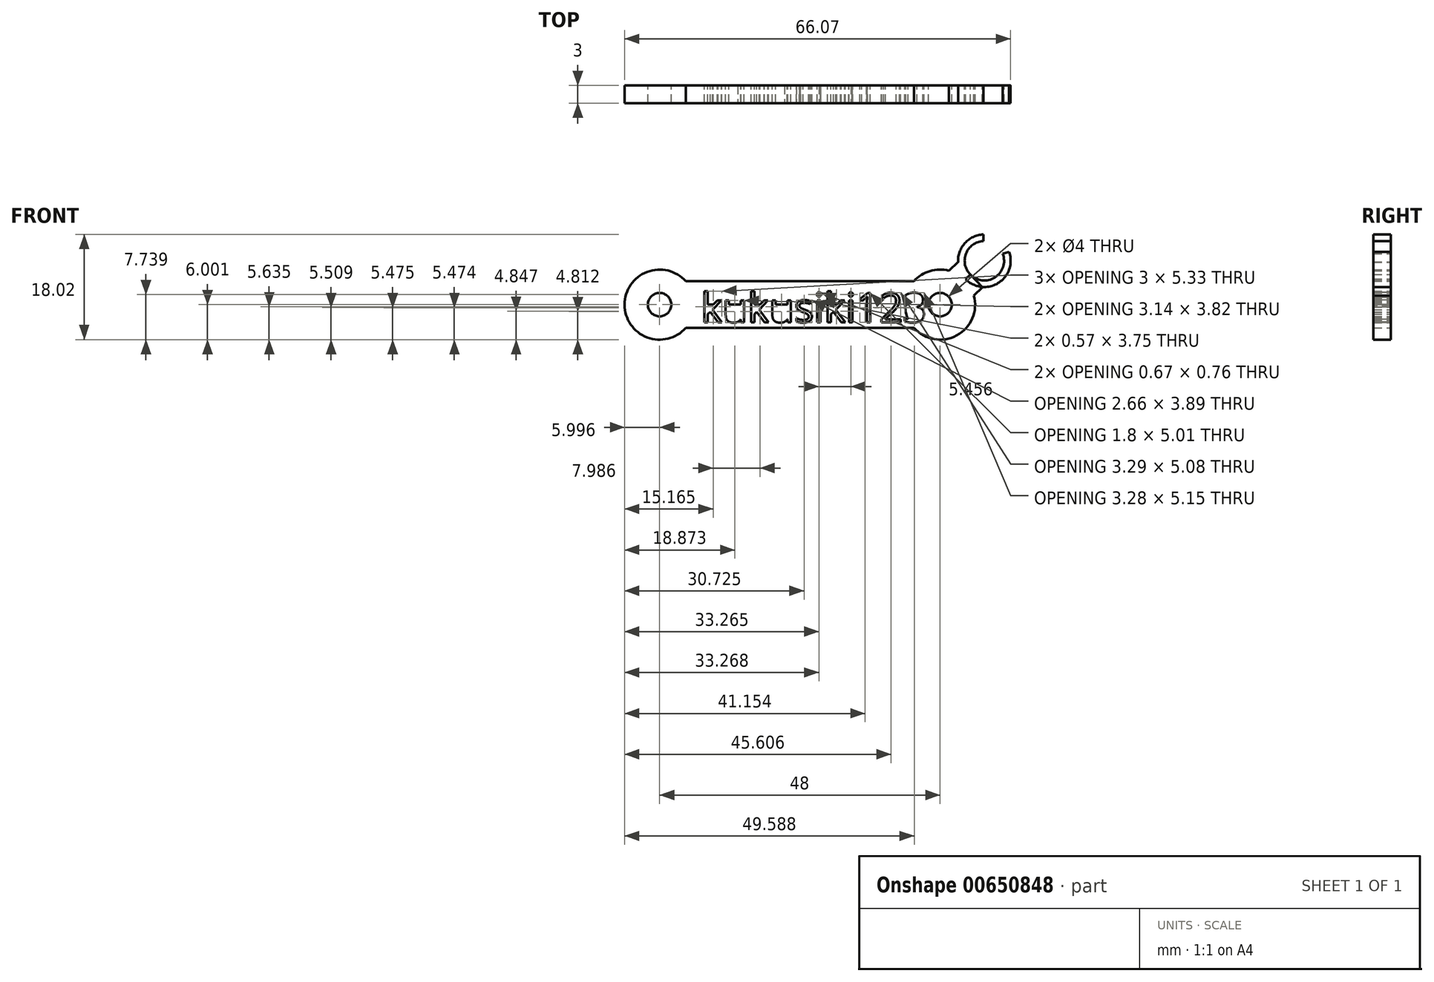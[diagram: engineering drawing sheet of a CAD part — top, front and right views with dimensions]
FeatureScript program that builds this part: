
annotation { "Feature Type Name" : "Feature", "Feature Type Description" : "" }
export const myFeature = defineFeature(function(context is Context, id is Id, definition is map)
    precondition{}
    {
        {
            var Q0;
            Q0=qCreatedBy(makeId("Front.planeOp"),FACE);
            var sketch = newSketch(context, id + "F0", { "sketchPlane" : qUnion([Q0])});
            skCircle(sketch, "E0", {"center": v(-25.43, 16.93) * mm, "radius": 6 * mm});
            skLineSegment(sketch, "E1", {"start": v(-31.43, 16.93) * mm, "end": v(-27.43, 16.93) * mm});
            skCircle(sketch, "E2", {"center": v(-25.43, 16.93) * mm, "radius": 2 * mm});
            skLineSegment(sketch, "E3", {"start": v(-27.43, 16.93) * mm, "end": v(-69.43, 16.93) * mm});
            skLineSegment(sketch, "E4", {"start": v(-27.43, 16.93) * mm, "end": v(-27.43, 20.93) * mm});
            skLineSegment(sketch, "E5", {"start": v(-27.43, 20.93) * mm, "end": v(-27.43, 12.93) * mm});
            skLineSegment(sketch, "E6", {"start": v(-27.43, 12.93) * mm, "end": v(-69.43, 12.93) * mm});
            skLineSegment(sketch, "E7", {"start": v(-69.43, 12.93) * mm, "end": v(-69.43, 16.93) * mm});
            skLineSegment(sketch, "E8", {"start": v(-69.43, 20.93) * mm, "end": v(-69.43, 16.93) * mm});
            skLineSegment(sketch, "E9", {"start": v(-69.43, 20.93) * mm, "end": v(-27.43, 20.93) * mm});
            skLineSegment(sketch, "E10", {"start": v(-69.43, 16.93) * mm, "end": v(-73.43, 16.93) * mm});
            skCircle(sketch, "E11", {"center": v(-73.43, 16.93) * mm, "radius": 6 * mm});
            skCircle(sketch, "E12", {"center": v(-73.43, 16.93) * mm, "radius": 2 * mm});
            skLineSegment(sketch, "E13", {"start": v(-25.43, 16.93) * mm, "end": v(-21.2, 21.18) * mm});
            skLineSegment(sketch, "E14", {"start": v(-21.2, 21.18) * mm, "end": v(-20.27, 22.09) * mm});
            skLineSegment(sketch, "E15", {"start": v(-20.27, 22.09) * mm, "end": v(-18.17, 19.95) * mm});
            skLineSegment(sketch, "E16", {"start": v(-18.17, 19.95) * mm, "end": v(-22.37, 24.23) * mm});
            skLineSegment(sketch, "E17", {"start": v(-22.37, 24.23) * mm, "end": v(-23.9, 22.73) * mm});
            skLineSegment(sketch, "E18", {"start": v(-18.17, 19.95) * mm, "end": v(-19.64, 18.5) * mm});
            skLineSegment(sketch, "E19", {"start": v(-20.27, 22.09) * mm, "end": v(-17.86, 24.45) * mm});
            skCircle(sketch, "E20", {"center": v(-17.86, 24.45) * mm, "radius": 3.38 * mm});
            skCircle(sketch, "E21", {"center": v(-17.86, 24.45) * mm, "radius": 4.5 * mm});
            skLineSegment(sketch, "E22", {"start": v(-18.04, 27.82) * mm, "end": v(-14.7, 25.63) * mm});
            skLineSegment(sketch, "E23", {"start": v(-14.7, 25.63) * mm, "end": v(-13.61, 25.94) * mm});
            skLineSegment(sketch, "E24", {"start": v(-18.04, 27.82) * mm, "end": v(-18.04, 28.95) * mm});
            skText(sketch, "E25", { "text": "kukusiki123", "fontName": "OpenSans-Regular.ttf"});
            const initialGuessF0  = {"E25": [-0.06637, 0.0139, 1, 0, 0.00505]};
            skSetInitialGuess(sketch, initialGuessF0);
            skSolve(sketch);
        }
        {
            var Q0;
            {var subQ4=sQuery(id+"F0.wireOp",EDGE,"E7");Q0=makeQuery(id+"F0.imprint","IMPRINT",FACE,{"disambiguationData":[TD([[makeQuery(id+"F0.imprint","IMPRINT",EDGE,{"derivedFrom":subQ4}),1.0]])]});}
            var Q1;
            {var subQ0=sQuery(id+"F0.wireOp",EDGE,"E7");Q1=makeQuery(id+"F0.imprint","IMPRINT",FACE,{"disambiguationData":[TD([[makeQuery(id+"F0.imprint","IMPRINT",EDGE,{"derivedFrom":subQ0}),-1.0]])]});}
            var Q2;
            {var subQ0=sQuery(id+"F0.wireOp",EDGE,"E8");Q2=makeQuery(id+"F0.imprint","IMPRINT",FACE,{"disambiguationData":[TD([[makeQuery(id+"F0.imprint","IMPRINT",EDGE,{"derivedFrom":subQ0}),1.0]])]});}
            var Q3;
            {var subQ0=sQuery(id+"F0.wireOp",EDGE,"E9");var subQ1=sQuery(id+"F0.wireOp",EDGE,"E0");var subQ2=makeQuery(id+"F0.imprint","INTERSECT",VERTEX,{"derivedFrom":[subQ1,subQ0]});Q3=makeQuery(id+"F0.imprint","IMPRINT",FACE,{"disambiguationData":[TD([[makeQuery(id+"F0.imprint","IMPRINT",EDGE,{"disambiguationData":[TD([[subQ2,-1.0]])],"derivedFrom":subQ1}),-1.0]])]});}
            var Q4;
            {var subQ0=sQuery(id+"F0.wireOp",EDGE,"E6");var subQ1=sQuery(id+"F0.wireOp",EDGE,"E0");var subQ2=makeQuery(id+"F0.imprint","INTERSECT",VERTEX,{"derivedFrom":[subQ1,subQ0]});Q4=makeQuery(id+"F0.imprint","IMPRINT",FACE,{"disambiguationData":[TD([[makeQuery(id+"F0.imprint","IMPRINT",EDGE,{"disambiguationData":[TD([[subQ2,1.0]])],"derivedFrom":subQ1}),-1.0]])]});}
            var Q5;
            {var subQ0=sQuery(id+"F0.wireOp",EDGE,"E9");var subQ1=sQuery(id+"F0.wireOp",EDGE,"E0");var subQ2=makeQuery(id+"F0.imprint","INTERSECT",VERTEX,{"derivedFrom":[subQ1,subQ0]});Q5=makeQuery(id+"F0.imprint","IMPRINT",FACE,{"disambiguationData":[TD([[makeQuery(id+"F0.imprint","IMPRINT",EDGE,{"disambiguationData":[TD([[subQ2,-1.0]])],"derivedFrom":subQ1}),1.0]])]});}
            var Q6;
            {var subQ0=sQuery(id+"F0.wireOp",EDGE,"E6");var subQ1=sQuery(id+"F0.wireOp",EDGE,"E0");var subQ2=makeQuery(id+"F0.imprint","INTERSECT",VERTEX,{"derivedFrom":[subQ1,subQ0]});Q6=makeQuery(id+"F0.imprint","IMPRINT",FACE,{"disambiguationData":[TD([[makeQuery(id+"F0.imprint","IMPRINT",EDGE,{"disambiguationData":[TD([[subQ2,1.0]])],"derivedFrom":subQ1}),1.0]])]});}
            var Q7;
            {var subQ7=sQuery(id+"F0.wireOp",EDGE,"E0");var subQ8=makeQuery(id+"F0.imprint","INTERSECT",VERTEX,{"derivedFrom":[subQ7,sQuery(id+"F0.wireOp",EDGE,"E18")]});Q7=makeQuery(id+"F0.imprint","IMPRINT",FACE,{"disambiguationData":[TD([[makeQuery(id+"F0.imprint","IMPRINT",EDGE,{"disambiguationData":[TD([[subQ8,1.0]])],"derivedFrom":subQ7}),1.0]])]});}
            var Q8;
            {var subQ0=sQuery(id+"F0.wireOp",EDGE,"E0");var subQ1=makeQuery(id+"F0.imprint","INTERSECT",VERTEX,{"derivedFrom":[subQ0,sQuery(id+"F0.wireOp",EDGE,"E17")]});Q8=makeQuery(id+"F0.imprint","IMPRINT",FACE,{"disambiguationData":[TD([[makeQuery(id+"F0.imprint","IMPRINT",EDGE,{"disambiguationData":[TD([[subQ1,-1.0]])],"derivedFrom":subQ0}),1.0]])]});}
            var Q9;
            {var subQ5=sQuery(id+"F0.wireOp",EDGE,"E23");Q9=makeQuery(id+"F0.imprint","IMPRINT",FACE,{"disambiguationData":[TD([[makeQuery(id+"F0.imprint","IMPRINT",EDGE,{"derivedFrom":subQ5}),-1.0]])]});}
            var Q10;
            {var subQ5=sQuery(id+"F0.wireOp",EDGE,"E24");Q10=makeQuery(id+"F0.imprint","IMPRINT",FACE,{"disambiguationData":[TD([[makeQuery(id+"F0.imprint","IMPRINT",EDGE,{"derivedFrom":subQ5}),1.0]])]});}
            var Q11;
            {var subQ0=sQuery(id+"F0.wireOp",EDGE,"E16");var subQ3=sQuery(id+"F0.wireOp",EDGE,"E21");var subQ5=makeQuery(id+"F0.imprint","INTERSECT",VERTEX,{"disambiguationData":[OD(1.0)],"derivedFrom":[subQ0,subQ3]});Q11=makeQuery(id+"F0.imprint","IMPRINT",FACE,{"disambiguationData":[TD([[makeQuery(id+"F0.imprint","IMPRINT",EDGE,{"disambiguationData":[TD([[subQ5,-1.0]])],"derivedFrom":subQ3}),1.0]])]});}
            var Q12;
            {var subQ0=sQuery(id+"F0.wireOp",EDGE,"E16");var subQ3=sQuery(id+"F0.wireOp",EDGE,"E21");var subQ5=makeQuery(id+"F0.imprint","INTERSECT",VERTEX,{"disambiguationData":[OD(0.0)],"derivedFrom":[subQ0,subQ3]});Q12=makeQuery(id+"F0.imprint","IMPRINT",FACE,{"disambiguationData":[TD([[makeQuery(id+"F0.imprint","IMPRINT",EDGE,{"disambiguationData":[TD([[subQ5,1.0]])],"derivedFrom":subQ3}),1.0]])]});}
            var Q13;
            {var subQ0=sQuery(id+"F0.wireOp",EDGE,"E17");Q13=makeQuery(id+"F0.imprint","IMPRINT",FACE,{"disambiguationData":[TD([[makeQuery(id+"F0.imprint","IMPRINT",EDGE,{"derivedFrom":subQ0}),1.0]])]});}
            var Q14;
            {var subQ0=sQuery(id+"F0.wireOp",EDGE,"E18");Q14=makeQuery(id+"F0.imprint","IMPRINT",FACE,{"disambiguationData":[TD([[makeQuery(id+"F0.imprint","IMPRINT",EDGE,{"derivedFrom":subQ0}),-1.0]])]});}
            extrude(context, id + "F1", {"entities" : qUnion([Q0, Q1, Q2, Q3, Q4, Q5, Q6, Q7, Q8, Q9, Q10, Q11, Q12, Q13, Q14]), "depth" : 3 * mm, "offsetDistance" : 25 * mm});
        }
    });
